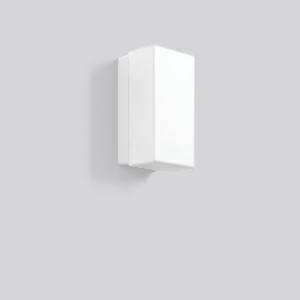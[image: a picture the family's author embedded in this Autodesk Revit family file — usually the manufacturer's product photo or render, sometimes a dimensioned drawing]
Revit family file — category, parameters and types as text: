
# Revit family: rechteck_21146_002_7167
name_source: partatom
category: Lighting Fixtures
units: mm (PartAtom-declared; Revit-internal decimal feet)

## family parameters
Cut with Voids When Loaded = No
Host = Face
Light Source = No
Part Type = Normal
Room Calculation Point = No
Round Connector Dimension = Use Diameter
Shared = No

## types (1)
- RECHTECK (1 x QA60/clear E27, 700 lm, 46 W, 3000)
    Apparent Load = 46 VA
    CIE Flux Codes = 35 64 86 74 50
    Color Rendering = 90
    Color Temperature = 3000
    Default Elevation = 1800 mm
    Description = Series: RECHTECK
Rectangular surface-mounted luminaire in classic design. Base: plastic. Opal glass: mouth-blown, satin finish. Diffuser fastening: spring system. Suitable for Ceiling mounting, Wall (surface). IP 43 ceiling mounting, IP 44 wall mounting. 
Colour: white
Length: 220 mm
Width: 120 mm
Height: 105 mm
Lamp: A60
Number of lamps: 1
Wattage: 60 W
Socket: E27
System power: 46 W
Rated luminous flux: 350 lm
Luminous efficiency: 8 lm/W
Control gear: Converter not necessary
Protection class: II
Type of protection: IP 43
    Height = 105 mm
    Lamp = 1 x QA60/clear E27
    Lamp Light Flux = 700 lm
    Lamp Power = 46 W
    Lamp count = 1
    Length = 220 mm
    Lifetime = 3000 h
    Luminous efficacy = 8 lm/W
    Manufacturer = RZB
    ModVariant = No
    Model = 21146.002
    Mounting Place = Ceiling, Wall
    Mounting Type = Surface mounted
    Number of Poles = 1
    OnlyDefault = Yes
    Power Factor = 1
    Product Name = RECHTECK
    Product group = Surface mounted ceiling and wall luminaires
    ProductGroupID = 305
    Protection Class = Protection class II
    Protection Degree = IP 43
    RLX_Detail_Level = 1
    RLX_Emergency_Light_Flux = 0 lm
    RLX_Emergency_Type = 0
    RLX_Emergency_Type_DB = No
    RlxData = <blob elided: 19409 chars, md5=9a3f0556>
    Socket = E27
    Standby Power = 0 W
    System Light Flux = 352 lm
    System Power = 46 W
    Type Comments = Product without accessories
    Type Image = 21146.002.jpg
    URL = http://relux.com
    VarID = ---
    Voltage = 230 V
    Voltage Range = 220-240 V
    Weight = 0.00 kg
    Width = 120 mm

## geometry (parser evidence)
native form markers: Blend x4, Sweep x13
no freeform markers — native parametric forms only
